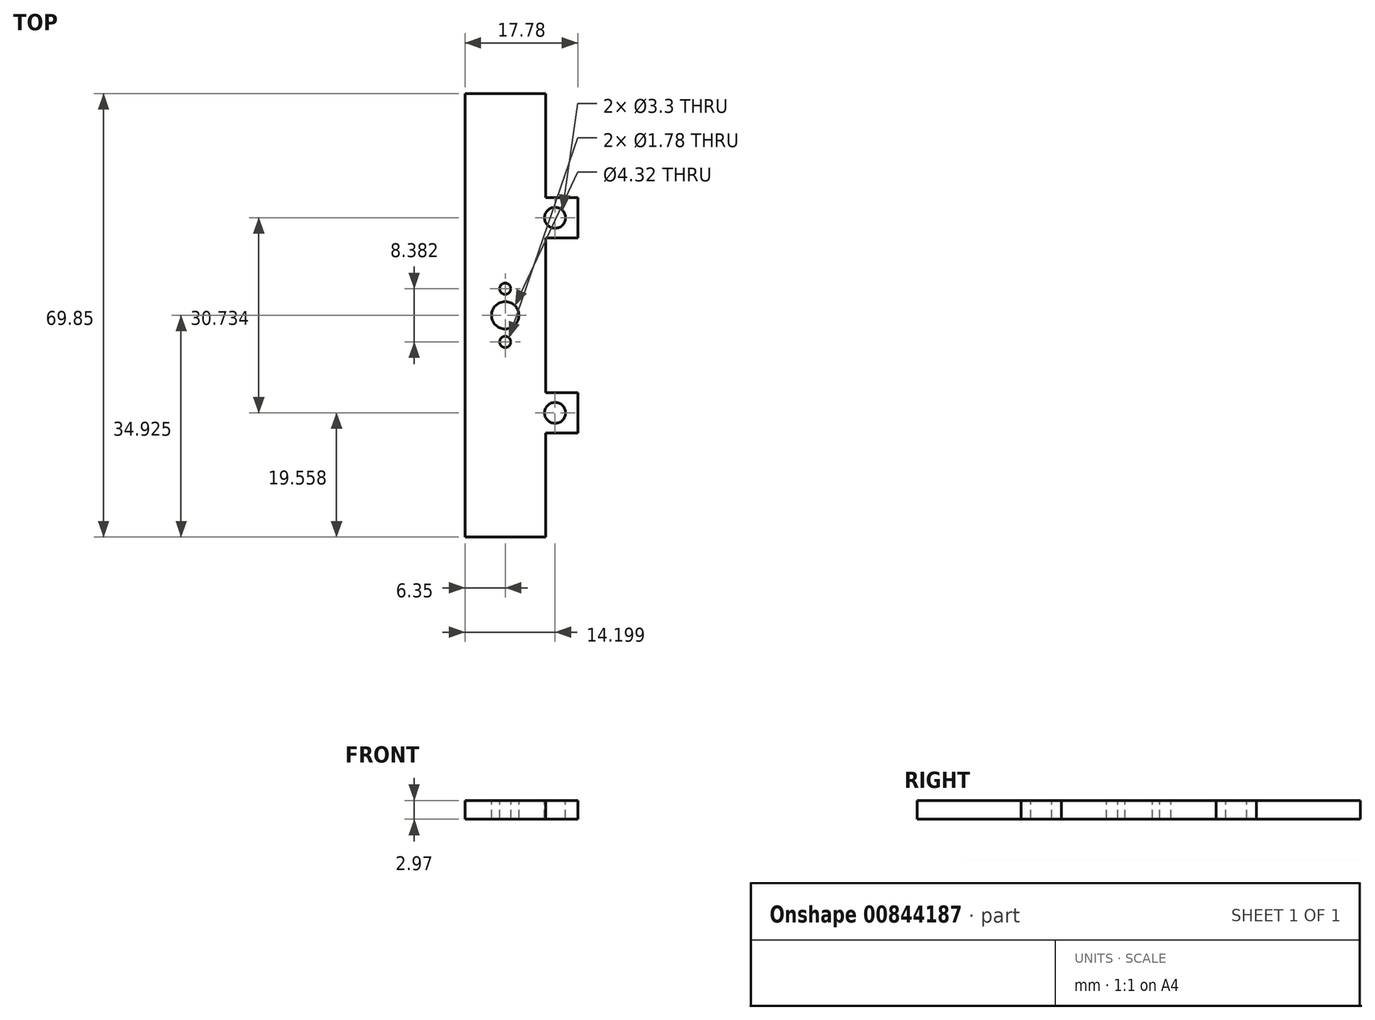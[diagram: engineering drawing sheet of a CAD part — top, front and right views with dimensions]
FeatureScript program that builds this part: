
annotation { "Feature Type Name" : "Feature", "Feature Type Description" : "" }
export const myFeature = defineFeature(function(context is Context, id is Id, definition is map)
    precondition{}
    {
        {
            var Q0;
            Q0=qCreatedBy(makeId("Top.planeOp"),FACE);
            var sketch = newSketch(context, id + "F0", { "sketchPlane" : qUnion([Q0])});
            skLineSegment(sketch, "E0.bottom", {"start": v(0, 0) * mm, "end": v(12.7, 0) * mm});
            skLineSegment(sketch, "E0.top", {"start": v(0, 69.85) * mm, "end": v(12.7, 69.85) * mm});
            skLineSegment(sketch, "E0.left", {"start": v(0, 0) * mm, "end": v(0, 69.85) * mm});
            skLineSegment(sketch, "E0.right", {"start": v(12.7, 0) * mm, "end": v(12.7, 16.38) * mm});
            skLineSegment(sketch, "E1.bottom", {"start": v(12.7, 53.47) * mm, "end": v(17.78, 53.47) * mm});
            skLineSegment(sketch, "E1.top", {"start": v(12.7, 47.12) * mm, "end": v(17.78, 47.12) * mm});
            skLineSegment(sketch, "E1.right", {"start": v(17.78, 53.47) * mm, "end": v(17.78, 47.12) * mm});
            skLineSegment(sketch, "E2.bottom", {"start": v(12.7, 22.73) * mm, "end": v(17.78, 22.73) * mm});
            skLineSegment(sketch, "E2.top", {"start": v(12.7, 16.38) * mm, "end": v(17.78, 16.38) * mm});
            skLineSegment(sketch, "E2.right", {"start": v(17.78, 22.73) * mm, "end": v(17.78, 16.38) * mm});
            skLineSegment(sketch, "E3.trimOffspring", {"start": v(12.7, 53.47) * mm, "end": v(12.7, 69.85) * mm});
            skLineSegment(sketch, "E4.trimOffspring", {"start": v(12.7, 22.73) * mm, "end": v(12.7, 47.12) * mm});
            skSolve(sketch);
        }
        {
            var Q0;
            Q0 = qSketchRegion(id + "F0", true);
            extrude(context, id + "F1", {"entities" : qUnion([Q0]), "depth" : 2.97 * mm, "offsetDistance" : 25.4 * mm});
        }
        {
            var Q0;
            Q0=makeQuery(id+"F1.opExtrude","CAP_FACE",FACE,{"disambiguationData":[OSD([sQuery(id+"F0.wireOp",EDGE,"E0.bottom"),sQuery(id+"F0.wireOp",EDGE,"E0.top"),sQuery(id+"F0.wireOp",EDGE,"E0.left"),sQuery(id+"F0.wireOp",EDGE,"E0.right"),sQuery(id+"F0.wireOp",EDGE,"E1.bottom"),sQuery(id+"F0.wireOp",EDGE,"E1.top"),sQuery(id+"F0.wireOp",EDGE,"E1.right"),sQuery(id+"F0.wireOp",EDGE,"E2.bottom"),sQuery(id+"F0.wireOp",EDGE,"E2.top"),sQuery(id+"F0.wireOp",EDGE,"E2.right"),sQuery(id+"F0.wireOp",EDGE,"E3.trimOffspring"),sQuery(id+"F0.wireOp",EDGE,"E4.trimOffspring")])],"isStart":false});
            var sketch = newSketch(context, id + "F2", { "sketchPlane" : qUnion([Q0])});
            skCircle(sketch, "E5", {"center": v(14.2, 50.3) * mm, "radius": 1.65 * mm});
            skCircle(sketch, "E6", {"center": v(14.2, 19.56) * mm, "radius": 1.65 * mm});
            skCircle(sketch, "E7", {"center": v(6.35, 34.93) * mm, "radius": 2.16 * mm});
            skCircle(sketch, "E8", {"center": v(6.35, 39.12) * mm, "radius": 0.89 * mm});
            skCircle(sketch, "E9", {"center": v(6.35, 30.73) * mm, "radius": 0.89 * mm});
            skSolve(sketch);
        }
        {
            var Q0;
            Q0 = qSketchRegion(id + "F2", true);
            extrude(context, id + "F3", {"entities" : qUnion([Q0]), "operationType" : NewBodyOperationType.REMOVE, "oppositeDirection" : true, "depth" : 25.4 * mm, "offsetDistance" : 25.4 * mm});
        }
    });
